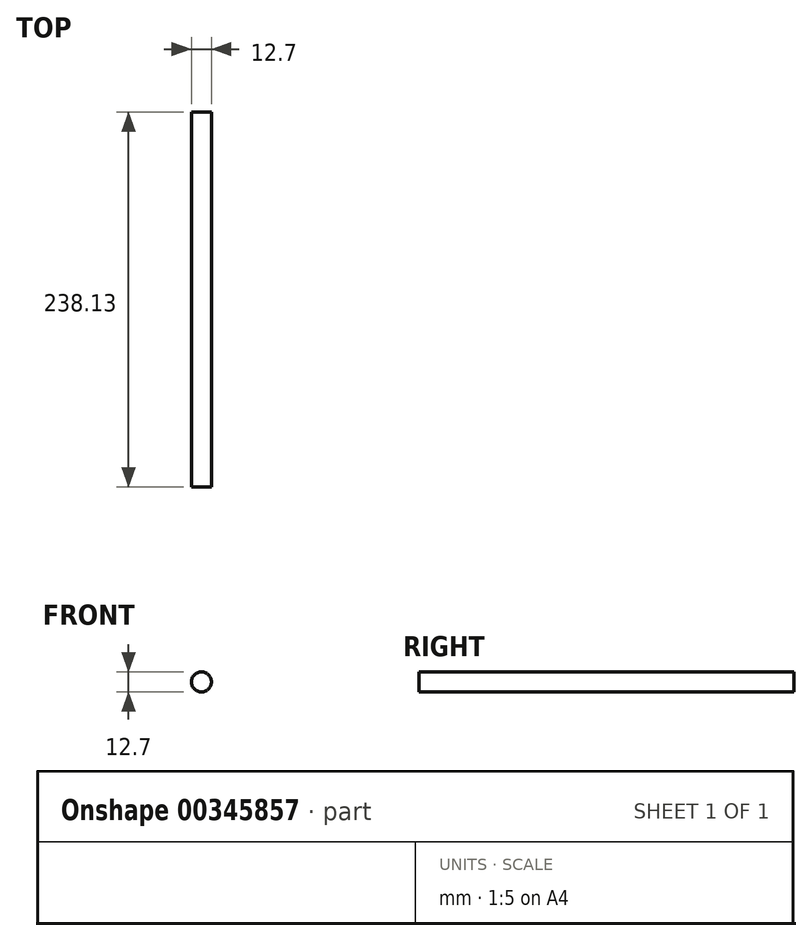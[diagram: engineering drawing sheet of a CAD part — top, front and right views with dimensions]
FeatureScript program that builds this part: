
annotation { "Feature Type Name" : "Feature", "Feature Type Description" : "" }
export const myFeature = defineFeature(function(context is Context, id is Id, definition is map)
    precondition{}
    {
        {
            var Q0;
            Q0=qCreatedBy(makeId("Front.planeOp"),FACE);
            var sketch = newSketch(context, id + "F0", { "sketchPlane" : qUnion([Q0])});
            skCircle(sketch, "E0", {"center": v(0, 0) * mm, "radius": 6.35 * mm});
            skSolve(sketch);
        }
        {
            var Q0;
            Q0=makeQuery(id+"F0.imprint","IMPRINT",FACE,{"disambiguationData":[TD([[makeQuery(id+"F0.imprint","IMPRINT",EDGE,{"derivedFrom":sQuery(id+"F0.wireOp",EDGE,"E0")}),1.0]])]});
            extrude(context, id + "F1", {"entities" : qUnion([Q0]), "depth" : 238.12 * mm});
        }
    });
